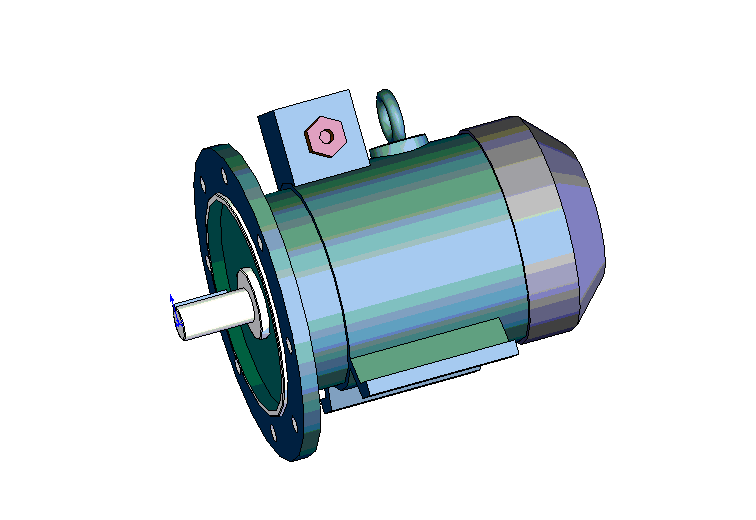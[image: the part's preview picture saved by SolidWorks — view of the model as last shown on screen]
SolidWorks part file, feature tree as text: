
SOLIDWORKS PART (.sldprt)
format: sldprt  version: not decoded by parser v0  size: 643,584 bytes
history: native  units: mm
features: sketch x18, extrude x12, plane x4, cut_extrude x4, chamfer x3, material x1, sweep x1 (+10 scaffold rows collapsed)
feature tree (53):
  scaffold x10  (default folders/planes/origin — collapsed)
  material  "Ст.3 ГОСТ 380-88"
  plane  "Спереди"
  plane  "Сверху"
  plane  "Справа"
  sketch  "Эскиз1"  dims[D1=38.0mm]
  extrude  "Вытянуть1"  Depth=80mm
  sketch  "Эскиз2"  dims[D1=8.0mm D2=8.0mm D3=41.0mm]
  extrude  "Вытянуть2"  Depth=60mm
  sketch  "Эскиз3"  dims[D1=350.0mm]
  extrude  "Вытянуть3"  Depth=19mm
  sketch  "Эскиз4"  dims[D1=250.0mm D2=236.0mm]
  extrude  "Вытянуть4"  Depth=5mm
  sketch  "Эскиз5"  dims[D1=236.0mm D2=80.0mm]
  cut_extrude  "Вырез-Вытянуть1"  Depth=10mm
  chamfer  "Фаска1"  Distance=1mm Angle=45deg
  sketch  "Эскиз6"  dims[c1.D2=19.0mm c1.D1=~202.320481mm c2.D1=22.5deg c2.D3=150.0mm c2.D4=150.0mm c2.D5=150.0mm]
  cut_extrude  "Вырез-Вытянуть2"  [1 undecoded]
  sketch  "Эскиз7"  dims[D1=220.0mm]
  extrude  "Вытянуть5"  Depth=55mm
  sketch  "Эскиз8"  dims[D1=232.0mm]
  extrude  "Вытянуть6"  Depth=204mm
  sketch  "Эскиз9"  dims[D1=240.0mm]
  extrude  "Вытянуть7"  Depth=102mm
  chamfer  "Фаска2"  Distance=45mm Angle=45deg
  sketch  "Эскиз10"  dims[c1.D1=16.0mm c1.D2=16.0mm c1.D3=~78.208589mm c2.D3=30.0deg c2.D4=123.0mm c2.D5=30.0mm c2.D6=132.0mm c2.D7=105.0mm]
  extrude  "Вытянуть8"  Depth=170mm
  sketch  "Эскиз11"  dims[c1.D2=19.0mm c1.D1=169.0mm c1.D3=108.0mm c1.D4=90.0deg c1.D5=309.0mm c1.D6=216.0mm c1.D7=140.0mm c2.D6=~140.862792deg]
  cut_extrude  "Вырез-Вытянуть3"  [1 undecoded]
  sketch  "Эскиз12"  dims[D1=1.0mm D2=86.0mm D3=86.0mm]
  extrude  "Вытянуть9"  Depth=193mm
  sketch  "Эскиз13"  dims[D1=64.0mm D2=286.0mm]
  extrude  "Вытянуть10"  Depth=126mm
  chamfer  "Фаска3"  Distance=1mm Angle=45deg
  plane  "Плоскость1"  Offset=286mm
  sketch  "Эскиз14"  dims[D1=52.0mm]
  sketch  "Эскиз15"  dims[D1=14.0mm D2=52.0mm]
  sweep  "По траектории1"
  sketch  "Эскиз16"  dims[D1=30.0mm D2=43.0mm D3=43.0mm]
  extrude  "Вытянуть11"  Depth=10mm
  sketch  "Эскиз17"  dims[D1=19.5mm]
  extrude  "Вытянуть12"  Depth=15mm
  sketch  "Эскиз18"  dims[D1=16.0mm]
  cut_extrude  "Вырез-Вытянуть4"  Depth=15mm
decode coverage: 35 of 38 modeling features carry decoded parameters
note: ~ marks probable driven/reference dimensions
note: 2 parameter values undecoded
note: suppression state not decoded; provenance and decode notes live in map.json
